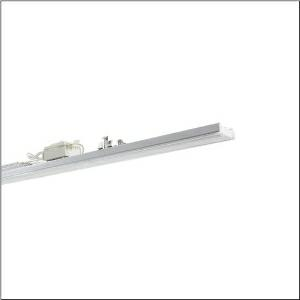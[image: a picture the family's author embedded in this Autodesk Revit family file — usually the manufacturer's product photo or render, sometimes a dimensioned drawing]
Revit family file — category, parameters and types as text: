
# Revit family: licross_11_recessed_ho_51te12dv4m2m
name_source: partatom
category: Lighting Fixtures
units: mm (PartAtom-declared; Revit-internal decimal feet)

## family parameters
Cut with Voids When Loaded = No
Host = Face
Light Source = No
Part Type = Normal
Room Calculation Point = No
Round Connector Dimension = Use Diameter
Shared = No

## types (1)
- --- (1 x LED, 27150 lm, 150.5 W, 4000K)
    Apparent Load = 150 VA
    CIE Flux Codes = 66 91 98 100 100
    Color Rendering = 80
    Color Temperature = 4000K
    Default Elevation = 1800 mm
    Description = Licross 11 Recessed HO, luminaire insert, of sheet steel, galvanised, coil coated, white, length: 2.250mm, width: 66mm, height: 67mm, LED rated luminous flux: 27.150lm, light colour: 840, SDCM (Standard Deviation of Colour Matching)MacAdam ≤ 2 SDCM (initial), control gear: DALI 2, with plug, 5-pole, with phase selection, mains connection: 220..240V, AC, 50/60Hz, rated input power: 151W, internal wiring halogen-free, primary optical cover: cover, of PMMA, light emission: direct distribution, primary light characteristic: symmetric, protection rating (complete): IP54, insulation class (complete): insulation class I (protective earthing), certification: CE, ENEC, VDE, UKCA, protection symbol: D if used in an environment with non-conductive dust loads with corresponding accessories, impact resistance: IK06, permissible ambient temperature for indoor applications: -40..+35°C, corresponds to IFS (International Featured Standards) requirements for safety and quality in the food industry, reducing of maximum allowable ambient temperature of 5°C with ceiling mounting, LABS conformity tested according to VDMA 24364:2018-05, The light source and the operating device comply with the requirements of the Ecodesign Regulation (EU) 2019/2020 and are replaceable in accordance with this regulation, packaging unit: 1 piece
    Height = 58 mm
    Lamp = 1 x LED
    Lamp Light Flux = 27150 lm
    Lamp Power = 150.5 W
    Lamp count = 1
    Length = 2250 mm
    Luminous efficacy = 180 lm/W
    Manufacturer = Siteco
    ModVariant = No
    Model = 51TE12DV4M2M
    Mounting Place = Ceiling
    Mounting Type = Pendant
    Number of Poles = 1
    OnlyDefault = Yes
    Power Factor = 1
    Product Name = Licross 11 Recessed HO
    Product group = luminaire insert | ceiling pendant
    ProductGroupID = 901
    Protection Class = Protection class I
    Protection Degree = IP 54
    RLX_Detail_Level = 1
    RLX_Emergency_Light_Flux = 0 lm
    RLX_Emergency_Type = 0
    RLX_Emergency_Type_DB = No
    RlxData = <blob elided: 30121 chars, md5=aecc507b>
    Socket = socket
    Standby Power = 0 W
    System Light Flux = 27150 lm
    System Power = 150 W
    Type Comments = factory setting: luminous flux: 100 % | dim-lin: 254 | 690 mA
    Type Image = l_1296930.jpg
    URL = http://relux.com
    VarID = @adj_101067
    Voltage = 0 V
    Weight = 0.00 kg
    Width = 66 mm

## geometry (parser evidence)
native form markers: Blend x4, Sweep x11
no freeform markers — native parametric forms only
